# Revit family: SS10-3090-24V-MTM-BK
name_source: partatom
category: Lighting Fixtures
units: mm (PartAtom-declared; Revit-internal decimal feet)

## family parameters
Cut with Voids When Loaded = Yes
Host = Face
Light Source = Yes
Maintain Annotation Orientation = No
Part Type = Normal
Room Calculation Point = No
Round Connector Dimension = Use Diameter
Shared = No

## types (3) — shared parameters
CRI = 90
Color Filter = 16777215
Default Elevation = 0' - 0"
Dimming Lamp Color Temperature Shift = <None>
Input Voltage = 24VDC
Lamp = LED
Load Classification = Lighting
Manufacturer = Above All Lighting
Power Factor = 0.9
Tilt Angle = 60.00°
URL = https://www.abovealllighting.com
Wattage Comments = 10W

## per-type parameters (varying)
| type | Beam Angle | Model | Photometric Web File |
| SS-10W-3000K-18D | 18.00° | SS10-3090-24V-18-MTM-BK | SS10-3090-24V-18-MTM-BK.ies.IES |
| SS-10W-3000K-24D | 24.00° | SS10-3090-24V-24-MTM-BK | SS10-3090-24V-24-MTM-BK.ies.IES |
| SS-10W-3000K-36D | 36.00° | SS10-3090-24V-36-MTM-BK | SS10-3090-24V-36-MTM-BK.ies.IES |

## geometry (parser evidence)
native form markers: Sweep x3
no freeform markers — native parametric forms only
